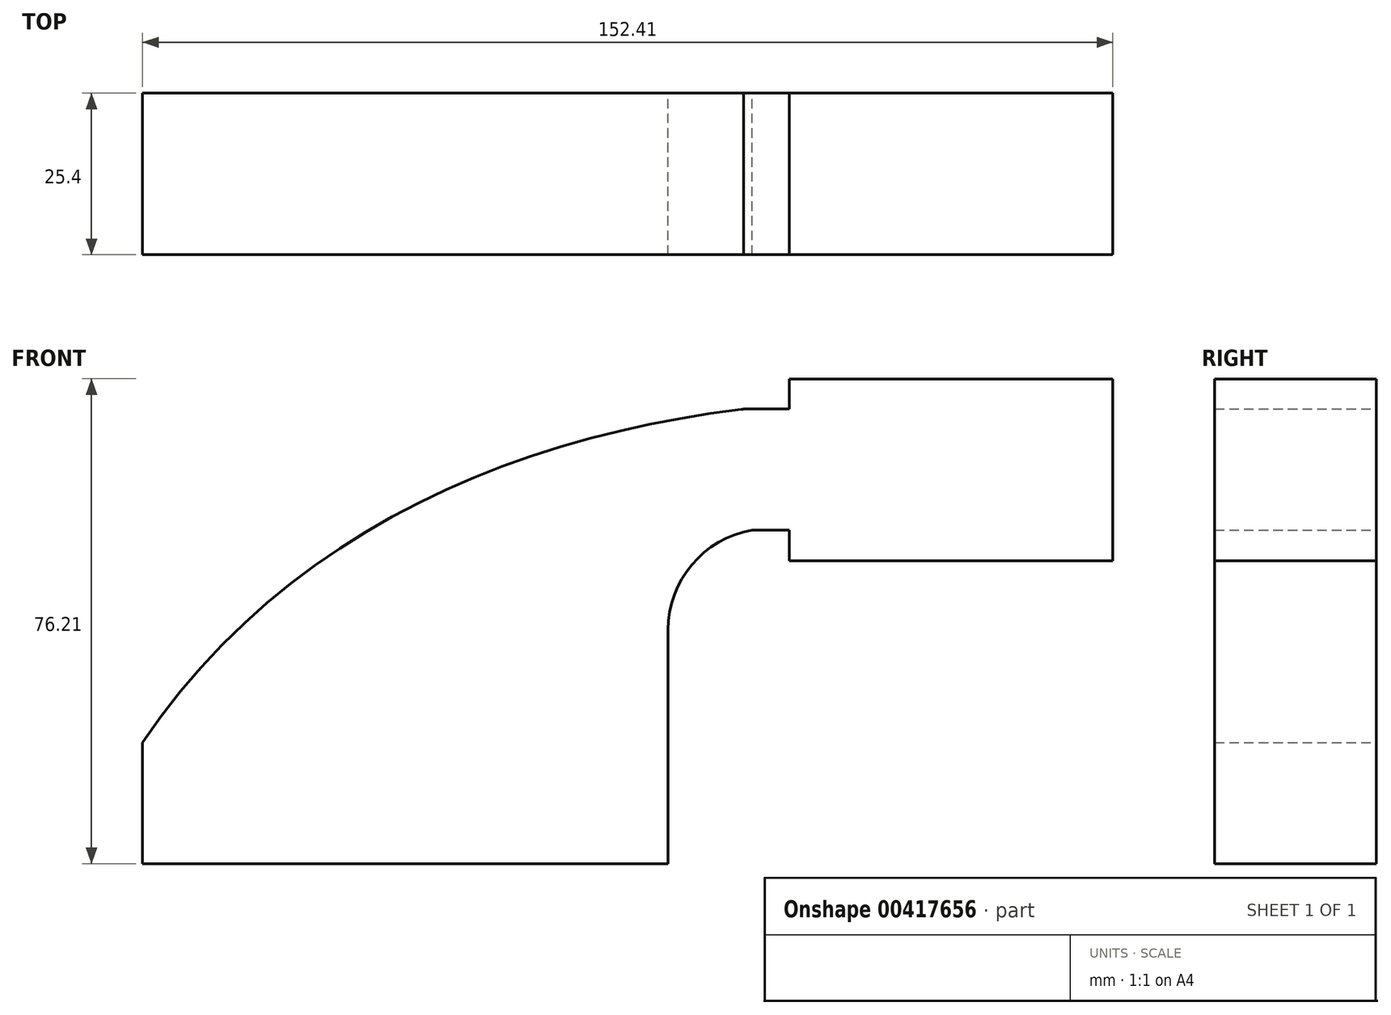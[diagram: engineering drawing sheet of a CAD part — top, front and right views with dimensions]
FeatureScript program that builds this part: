
annotation { "Feature Type Name" : "Feature", "Feature Type Description" : "" }
export const myFeature = defineFeature(function(context is Context, id is Id, definition is map)
    precondition{}
    {
        {
            var Q0;
            Q0=qCreatedBy(makeId("Front.planeOp"),FACE);
            var sketch = newSketch(context, id + "F0", { "sketchPlane" : qUnion([Q0])});
            skLineSegment(sketch, "E0.bottom", {"start": v(-41.28, 9.52) * mm, "end": v(41.28, 9.53) * mm});
            skLineSegment(sketch, "E0.top", {"start": v(-41.28, -9.53) * mm, "end": v(41.28, -9.53) * mm});
            skLineSegment(sketch, "E0.left", {"start": v(-41.28, 9.52) * mm, "end": v(-41.28, -9.53) * mm});
            skLineSegment(sketch, "E0.right", {"start": v(41.28, 9.53) * mm, "end": v(41.28, -9.52) * mm});
            skPoint(sketch, "E0.middle", {"position": v(0, 0) * mm});
            skLineSegment(sketch, "E1.bottom", {"start": v(60.33, 38.1) * mm, "end": v(111.13, 38.1) * mm});
            skLineSegment(sketch, "E1.top", {"start": v(60.33, 66.68) * mm, "end": v(111.12, 66.68) * mm});
            skLineSegment(sketch, "E1.left", {"start": v(60.33, 38.1) * mm, "end": v(60.32, 66.68) * mm});
            skLineSegment(sketch, "E1.right", {"start": v(111.12, 38.1) * mm, "end": v(111.12, 66.68) * mm});
            skPoint(sketch, "E1.middle", {"position": v(85.72, 52.39) * mm});
            skLineSegment(sketch, "E2", {"start": v(41.27, 9.53) * mm, "end": v(41.27, 27.23) * mm});
            skArc(sketch, "E3", {"start": v(41.27, 27.23) * mm, "mid": v(45, 37.46) * mm, "end": v(54.45, 42.88) * mm});
            skLineSegment(sketch, "E4", {"start": v(54.45, 42.88) * mm, "end": v(85.87, 42.88) * mm});
            skLineSegment(sketch, "E5.0", {"start": v(53.13, 61.93) * mm, "end": v(85.67, 61.93) * mm});
            skArc(sketch, "E5.1", {"start": v(22.22, 27.23) * mm, "mid": v(31.07, 50.46) * mm, "end": v(53.13, 61.93) * mm});
            skLineSegment(sketch, "E5.2", {"start": v(22.22, 9.53) * mm, "end": v(22.22, 27.23) * mm});
            skLineSegment(sketch, "E6", {"start": v(85.72, 38.1) * mm, "end": v(85.87, 66.68) * mm});
            skFitSpline(sketch, "E7", {"points": [v(-41.28, 9.52) * mm, v(53.13, 61.93) * mm], "startDerivative": vector(65.47, 97.02) * mm, "endDerivative": vector(111.7, 13.43) * mm});
            skSolve(sketch);
        }
        {
            var Q0;
            Q0 = qSketchRegion(id + "F0", true);
            extrude(context, id + "F1", {"entities" : qUnion([Q0]), "depth" : 25.4 * mm});
        }
    });
